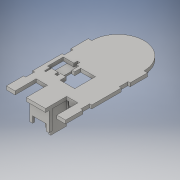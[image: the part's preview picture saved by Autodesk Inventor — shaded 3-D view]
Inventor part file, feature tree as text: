
AUTODESK INVENTOR PART (.ipt)
format: ipt  version: 2016 (Build 200138000, 138)  size: 553,472 bytes
history: native  units: in
note: dims shown in document units (in); Inventor stores cm internally (conversion verified against a paired STEP export)
features: reference x40, extrude x28, sketch x28, plane x6, projected_geometry x2
ambient origin geometry x8: Origin, YZ Plane, XZ Plane, XY Plane, X Axis, Y Axis, Z Axis, Center Point
bodies: Solid1 (feature_tree)
feature tree (104):
  extrude  "Extrusion1"  Depth=3.0in
  extrude  "Extrusion2"  Depth=0.0787in
  extrude  "Extrusion3"  Depth=1.0in
  extrude  "Extrusion5"  Depth=1.0in TaperAngle=0.0deg
  plane  "Work Plane1"
  extrude  "Extrusion6"  Depth=0.0787in
  extrude  "Extrusion9"  Depth=0.0787in
  extrude  "Extrusion14"  Depth=0.1575in
  extrude  "Extrusion15"  Depth=1.25in
  plane  "Work Plane2"
  extrude  "Extrusion16"  Depth=0.1575in
  extrude  "Extrusion17"  Depth=0.9201in TaperAngle=0.0deg
  extrude  "Extrusion18"  Depth=0.1969in
  plane  "Work Plane3"
  extrude  "Extrusion20"  Depth=0.1969in TaperAngle=0.0deg
  extrude  "Extrusion21"  Depth=0.1181in TaperAngle=0.0deg
  plane  "Work Plane4"
  plane  "Work Plane5"
  extrude  "Extrusion23"  Depth=0.1181in
  extrude  "Extrusion24"  Depth=0.1969in TaperAngle=0.0deg
  plane  "Work Plane6"
  extrude  "Extrusion25"  Depth=0.35in
  extrude  "Extrusion26"  Depth=0.2in
  extrude  "Extrusion27"  Depth=0.1969in TaperAngle=0.0deg
  extrude  "Extrusion28"  Depth=1.5in
  extrude  "Extrusion29"  Depth=0.7in
  extrude  "Extrusion30"  Depth=0.1181in TaperAngle=0.0deg
  extrude  "Extrusion31"  Depth=1.0in
  extrude  "Extrusion34"  Depth=0.5in
  sketch  "Sketch36"  dims[d105=0.1181in d106=0.5in]
  extrude  "Extrusion35"  Depth=0.5in
  extrude  "Extrusion36"  Depth=0.0197in
  extrude  "Extrusion37"  Depth=0.325in
  extrude  "Extrusion38"  Depth=0.1969in
  extrude  "Extrusion39"  Depth=0.1181in
  sketch  "Sketch41"  dims[d117=0.1969in d118=0.1181in d119=0.1969in d120=0.0in d121=0.1575in d122=0.0in d123=0.1in d124=0.0in d132=1.0in d133=0.0in d134=0.5in d135=0.5in d136=0.0039in d137=0.0039in d138=0.0984in d139=0.0984in d140=0.0039in d141=0.0984in d142=1.61in d143=0.0in d144=0.2in d145=0.0in d146=0.1181in d147=0.85in d148=0.0in d149=1.2in d150=0.1181in d151=1.1in d152=0.0in d153=0.28in d154=3.0in d155=0.0in]
  sketch  "Sketch1"  dims[d0=4.5in d1=3.0in]
  sketch  "Sketch2"  dims[d2=0.1969in d3=0.0in d5=0.0787in]
  reference  "Reference1"
  reference  "Reference2"
  sketch  "Sketch3"  dims[d6=1.0in d7=0.0in d8=1.0827in]
  sketch  "Sketch5"  dims[d9=0.3937in d10=1.0in d11=0.0in]
  reference  "Reference14"
  reference  "Reference15"
  reference  "Reference16"
  reference  "Reference17"
  reference  "Reference18"
  sketch  "Sketch6"  dims[d12=0.0787in d23=0.0098in]
  reference  "Reference19"
  sketch  "Sketch9"  dims[d24=0.1575in d25=0.0787in]
  projected_geometry  "Projected Loop2"
  sketch  "Sketch14"  dims[d26=0.0098in d27=0.1575in]
  sketch  "Sketch15"  dims[d28=0.1181in d29=0.0in d30=1.25in]
  sketch  "Sketch16"  dims[d31=0.1575in d32=0.1575in]
  reference  "Reference30"
  sketch  "Sketch17"  dims[d33=0.1181in d34=0.0in d46=0.9201in d47=0.0in]
  reference  "Reference31"
  reference  "Reference32"
  reference  "Reference33"
  reference  "Reference35"
  reference  "Reference36"
  reference  "Reference37"
  reference  "Reference38"
  reference  "Reference39"
  reference  "Reference40"
  reference  "Reference41"
  reference  "Reference42"
  reference  "Reference43"
  reference  "Reference44"
  reference  "Reference45"
  reference  "Reference46"
  reference  "Reference47"
  reference  "Reference48"
  reference  "Reference49"
  sketch  "Sketch20"  dims[d58=0.1969in d59=0.1969in]
  reference  "Reference50"
  sketch  "Sketch21"  dims[d60=0.1969in d61=0.1969in d62=0.0in]
  sketch  "Sketch23"  dims[d63=1.0in d64=0.0in d65=0.1181in d66=0.0in]
  reference  "Reference53"
  reference  "Reference54"
  sketch  "Sketch24"  dims[d67=0.1969in d68=0.0in d69=0.1181in]
  sketch  "Sketch25"  dims[d70=0.1181in d71=0.1969in d72=0.0in]
  reference  "Reference55"
  reference  "Reference56"
  sketch  "Sketch26"  dims[d75=0.0394in d76=0.35in]
  reference  "Reference57"
  reference  "Reference58"
  sketch  "Sketch28"  dims[d77=0.1628in d78=0.2in]
  sketch  "Sketch29"  dims[d79=0.0787in d80=0.0in d81=0.1969in d82=0.0in]
  sketch  "Sketch30"  dims[d89=1.5in d90=1.5in]
  reference  "Reference59"
  sketch  "Sketch31"  dims[d91=0.1181in d92=0.0in d93=0.7in]
  sketch  "Sketch32"  dims[d94=1.26in d95=0.0in d96=0.1181in d97=0.0in]
  sketch  "Sketch35"  dims[d98=0.1181in d99=0.0in d104=1.0in]
  reference  "Reference61"
  sketch  "Sketch37"  dims[d107=1.0in d108=0.5in]
  reference  "Reference62"
  sketch  "Sketch38"  dims[d109=10.0in d110=0.0in d111=0.0197in]
  reference  "Reference63"
  sketch  "Sketch39"  dims[d112=0.0197in d113=0.325in]
  reference  "Reference64"
  sketch  "Sketch40"  dims[d114=0.197in d115=0.0in d116=0.1969in]
  reference  "Reference65"
  projected_geometry  "Projected Loop6"
